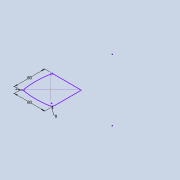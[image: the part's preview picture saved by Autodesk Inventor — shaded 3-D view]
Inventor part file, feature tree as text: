
AUTODESK INVENTOR PART (.ipt)
format: ipt  version: 2022 (Build 260153000, 153)  size: 71,680 bytes
history: native  units: mm
features: sketch x1
ambient origin geometry x8: Origin, YZ Plane, XZ Plane, XY Plane, X Axis, Y Axis, Z Axis, Center Point
feature tree (1):
  sketch  "Boceto1"  dims[d0=80.0mm d1=80.0mm d2=2.0mm d3=8.0mm]
